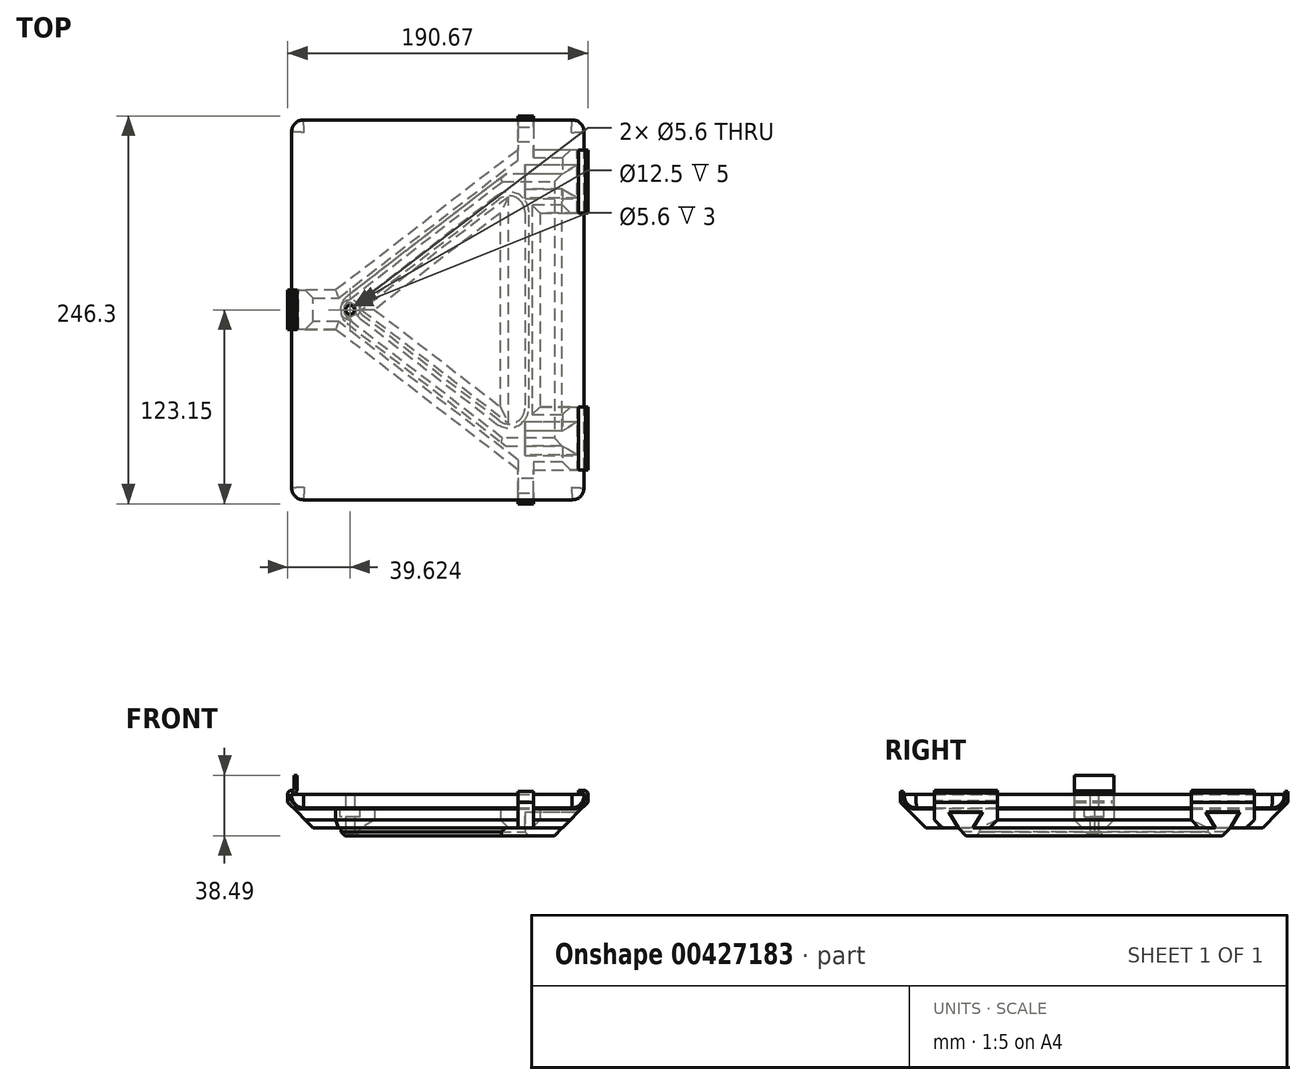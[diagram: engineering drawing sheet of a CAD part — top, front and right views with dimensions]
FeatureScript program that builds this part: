
annotation { "Feature Type Name" : "Feature", "Feature Type Description" : "" }
export const myFeature = defineFeature(function(context is Context, id is Id, definition is map)
    precondition{}
    {
        {
            var Q0;
            Q0=qCreatedBy(makeId("Top.planeOp"),FACE);
            var sketch = newSketch(context, id + "F0", { "sketchPlane" : qUnion([Q0])});
            skLineSegment(sketch, "E0.bottom", {"start": v(0, 0) * mm, "end": v(185.67, 0) * mm});
            skLineSegment(sketch, "E0.top", {"start": v(0, 241.3) * mm, "end": v(185.67, 241.3) * mm});
            skLineSegment(sketch, "E0.left", {"start": v(0, 0) * mm, "end": v(0, 241.3) * mm});
            skLineSegment(sketch, "E0.right", {"start": v(185.67, 0) * mm, "end": v(185.67, 241.3) * mm});
            skSolve(sketch);
        }
        {
            var Q0;
            Q0 = qSketchRegion(id + "F0", true);
            extrude(context, id + "F1", {"entities" : qUnion([Q0]), "depth" : 8.64 * mm});
        }
        {
            var Q0;
            Q0=makeQuery(id+"F1.opExtrude","SWEPT_EDGE",EDGE,{"disambiguationData":[OSD([sQuery(id+"F0.wireOp",EDGE,"E0.top"),sQuery(id+"F0.wireOp",EDGE,"E0.right")])]});
            var Q1;
            Q1=makeQuery(id+"F1.opExtrude","SWEPT_EDGE",EDGE,{"disambiguationData":[OSD([sQuery(id+"F0.wireOp",EDGE,"E0.top"),sQuery(id+"F0.wireOp",EDGE,"E0.left")])]});
            var Q2;
            Q2=makeQuery(id+"F1.opExtrude","SWEPT_EDGE",EDGE,{"disambiguationData":[OSD([sQuery(id+"F0.wireOp",EDGE,"E0.bottom"),sQuery(id+"F0.wireOp",EDGE,"E0.right")])]});
            var Q3;
            Q3=makeQuery(id+"F1.opExtrude","SWEPT_EDGE",EDGE,{"disambiguationData":[OSD([sQuery(id+"F0.wireOp",EDGE,"E0.bottom"),sQuery(id+"F0.wireOp",EDGE,"E0.left")])]});
            fillet(context, id + "F2", {"entities" : qUnion([Q0, Q1, Q2, Q3]), "radius" : 7.5 * mm, "tangentPropagation" : true, "allowEdgeOverflow" : false});
        }
        {
            var Q0;
            Q0=makeQuery(id+"F1.opExtrude","CAP_EDGE",EDGE,{"disambiguationData":[OSD([sQuery(id+"F0.wireOp",EDGE,"E0.right")])],"isStart":true});
            fillet(context, id + "F3", {"entities" : qUnion([Q0]), "radius" : 8 * mm, "tangentPropagation" : true, "allowEdgeOverflow" : false});
        }
        {
            var Q0;
            Q0=qCreatedBy(makeId("Front.planeOp"),FACE);
            cPlane(context, id + "F4", {"entities" : qUnion([Q0]), "cplaneType" : CPlaneType.OFFSET, "offset" : 120.65 * mm, "oppositeDirection" : true, "width" : 150 * mm, "height" : 150 * mm});
        }
        {
            var Q0;
            Q0=qCreatedBy(id+"F4.planeOp",FACE);
            var sketch = newSketch(context, id + "F5", { "sketchPlane" : qUnion([Q0])});
            skLineSegment(sketch, "E1.0.0", {"start": v(178.17, 8.64) * mm, "end": v(7.5, 8.64) * mm, "construction": true});
            skLineSegment(sketch, "E1.0.1", {"start": v(7.5, 8.64) * mm, "end": v(0, 8.64) * mm, "construction": true});
            skLineSegment(sketch, "E1.0.3", {"start": v(0, 8.64) * mm, "end": v(7.5, 8.64) * mm, "construction": true});
            skLineSegment(sketch, "E1.0.4", {"start": v(7.5, 8.64) * mm, "end": v(178.17, 8.64) * mm, "construction": true});
            skLineSegment(sketch, "E1.0.5", {"start": v(178.17, 8.64) * mm, "end": v(185.67, 8.64) * mm, "construction": true});
            skLineSegment(sketch, "E1.0.7", {"start": v(185.67, 8.64) * mm, "end": v(178.17, 8.64) * mm, "construction": true});
            skArc(sketch, "E2.0.0", {"start": v(8, 0) * mm, "mid": v(2.34, 2.34) * mm, "end": v(0, 8) * mm, "construction": true});
            skArc(sketch, "E2.0.2", {"start": v(0, 8) * mm, "mid": v(2.34, 2.34) * mm, "end": v(8, 0) * mm, "construction": true});
            skLineSegment(sketch, "E3.0.0", {"start": v(0, 8.64) * mm, "end": v(0, 8) * mm, "construction": true});
            skLineSegment(sketch, "E3.0.2", {"start": v(0, 8) * mm, "end": v(0, 8.64) * mm, "construction": true});
            skLineSegment(sketch, "E4.0.0", {"start": v(177.67, 0) * mm, "end": v(8, 0) * mm, "construction": true});
            skLineSegment(sketch, "E4.0.2", {"start": v(8, 0) * mm, "end": v(177.67, 0) * mm, "construction": true});
            skLineSegment(sketch, "E5", {"start": v(-0.2, 9.14) * mm, "end": v(1.8, 9.14) * mm});
            skLineSegment(sketch, "E6", {"start": v(-1.04, 11.14) * mm, "end": v(-2.5, 9.67) * mm});
            skLineSegment(sketch, "E7", {"start": v(-2.5, 9.67) * mm, "end": v(-2.5, 3.65) * mm});
            skLineSegment(sketch, "E8", {"start": v(3.65, -2.5) * mm, "end": v(8, -2.5) * mm});
            skLineSegment(sketch, "E9", {"start": v(8, -2.5) * mm, "end": v(8, -0.5) * mm});
            skLineSegment(sketch, "E10", {"start": v(-2.5, 3.65) * mm, "end": v(3.65, -2.5) * mm});
            skLineSegment(sketch, "E11", {"start": v(8, -0.5) * mm, "end": v(4.48, -0.5) * mm});
            skLineSegment(sketch, "E12", {"start": v(4.48, -0.5) * mm, "end": v(-0.5, 4.48) * mm});
            skLineSegment(sketch, "E13", {"start": v(-0.5, 4.48) * mm, "end": v(-0.5, 8.84) * mm});
            skLineSegment(sketch, "E14", {"start": v(-0.5, 8.84) * mm, "end": v(-0.2, 9.14) * mm});
            skLineSegment(sketch, "E15", {"start": v(1.8, 9.14) * mm, "end": v(3.5, 10.84) * mm});
            skLineSegment(sketch, "E16", {"start": v(3.5, 10.84) * mm, "end": v(3.5, 20.84) * mm});
            skLineSegment(sketch, "E17", {"start": v(3.5, 20.84) * mm, "end": v(1.5, 20.84) * mm});
            skLineSegment(sketch, "E18", {"start": v(1.5, 20.84) * mm, "end": v(1.5, 11.67) * mm});
            skLineSegment(sketch, "E19", {"start": v(1.5, 11.67) * mm, "end": v(0.96, 11.14) * mm});
            skLineSegment(sketch, "E20", {"start": v(-1.04, 11.14) * mm, "end": v(0.96, 11.14) * mm});
            skSolve(sketch);
        }
        {
            var Q0;
            Q0 = qSketchRegion(id + "F5", true);
            extrude(context, id + "F6", {"entities" : qUnion([Q0]), "endBound" : BoundingType.SYMMETRIC, "depth" : 25 * mm});
        }
        {
            var Q0;
            Q0=qCreatedBy(makeId("Front.planeOp"),FACE);
            cPlane(context, id + "F7", {"entities" : qUnion([Q0]), "cplaneType" : CPlaneType.OFFSET, "offset" : 19.05 * mm, "oppositeDirection" : true, "width" : 150 * mm, "height" : 150 * mm});
        }
        {
            var Q0;
            Q0=makeQuery(id+"F1.opExtrude","SWEPT_FACE",FACE,{"disambiguationData":[OSD([sQuery(id+"F0.wireOp",EDGE,"E0.top")])]});
            cPlane(context, id + "F8", {"entities" : qUnion([Q0]), "cplaneType" : CPlaneType.OFFSET, "offset" : 19.05 * mm, "oppositeDirection" : true, "width" : 150 * mm, "height" : 150 * mm});
        }
        {
            var Q0;
            Q0=qCreatedBy(id+"F7.planeOp",FACE);
            var sketch = newSketch(context, id + "F9", { "sketchPlane" : qUnion([Q0])});
            skEllipticalArc(sketch, "E21.0.0", {"construction": true});
            skLineSegment(sketch, "E21.0.1", {"start": v(178.17, 8) * mm, "end": v(7.5, 8) * mm, "construction": true});
            skEllipticalArc(sketch, "E21.0.2", {"construction": true});
            skLineSegment(sketch, "E21.0.3", {"start": v(177.67, 0) * mm, "end": v(8, 0) * mm, "construction": true});
            skLineSegment(sketch, "E22", {"start": v(92.84, 0) * mm, "end": v(92.84, 25) * mm, "construction": true});
            skPoint(sketch, "E22.endSnap0", {"position": v(92.84, 8) * mm});
            skLineSegment(sketch, "E23.0.0", {"start": v(8, -0.5) * mm, "end": v(4.48, -0.5) * mm, "construction": true});
            skLineSegment(sketch, "E23.0.1", {"start": v(4.48, -0.5) * mm, "end": v(-0.5, 4.48) * mm, "construction": true});
            skLineSegment(sketch, "E23.0.2", {"start": v(-0.5, 4.48) * mm, "end": v(-0.5, 8.84) * mm, "construction": true});
            skLineSegment(sketch, "E23.0.3", {"start": v(-0.5, 8.84) * mm, "end": v(-0.2, 9.14) * mm, "construction": true});
            skLineSegment(sketch, "E23.0.4", {"start": v(-0.2, 9.14) * mm, "end": v(1.8, 9.14) * mm, "construction": true});
            skLineSegment(sketch, "E23.0.5", {"start": v(1.8, 9.14) * mm, "end": v(3.5, 10.84) * mm, "construction": true});
            skLineSegment(sketch, "E23.0.6", {"start": v(3.5, 10.84) * mm, "end": v(3.5, 20.84) * mm, "construction": true});
            skLineSegment(sketch, "E23.0.7", {"start": v(3.5, 20.84) * mm, "end": v(1.5, 20.84) * mm, "construction": true});
            skLineSegment(sketch, "E23.0.8", {"start": v(1.5, 20.84) * mm, "end": v(1.5, 11.67) * mm, "construction": true});
            skLineSegment(sketch, "E23.0.9", {"start": v(1.5, 11.67) * mm, "end": v(0.96, 11.14) * mm, "construction": true});
            skLineSegment(sketch, "E23.0.10", {"start": v(0.96, 11.14) * mm, "end": v(-1.04, 11.14) * mm, "construction": true});
            skLineSegment(sketch, "E23.0.11", {"start": v(-1.04, 11.14) * mm, "end": v(-2.5, 9.67) * mm, "construction": true});
            skLineSegment(sketch, "E23.0.12", {"start": v(-2.5, 9.67) * mm, "end": v(-2.5, 3.65) * mm, "construction": true});
            skLineSegment(sketch, "E23.0.13", {"start": v(-2.5, 3.65) * mm, "end": v(3.65, -2.5) * mm, "construction": true});
            skLineSegment(sketch, "E23.0.14", {"start": v(3.65, -2.5) * mm, "end": v(8, -2.5) * mm, "construction": true});
            skLineSegment(sketch, "E23.0.15", {"start": v(8, -2.5) * mm, "end": v(8, -0.5) * mm, "construction": true});
            skLineSegment(sketch, "E24.MirrorCS", {"start": v(186.17, 8.84) * mm, "end": v(185.88, 9.14) * mm});
            skLineSegment(sketch, "E25.MirrorCS", {"start": v(185.88, 9.14) * mm, "end": v(184.7, 9.14) * mm});
            skLineSegment(sketch, "E26.MirrorCS", {"start": v(177.67, -2.5) * mm, "end": v(177.67, -0.5) * mm});
            skLineSegment(sketch, "E27.MirrorCS", {"start": v(177.67, -0.5) * mm, "end": v(181.2, -0.5) * mm});
            skLineSegment(sketch, "E28.MirrorCS", {"start": v(186.7, 11.14) * mm, "end": v(188.17, 9.67) * mm});
            skLineSegment(sketch, "E29.MirrorCS", {"start": v(184.7, 11.14) * mm, "end": v(186.7, 11.14) * mm});
            skLineSegment(sketch, "E30.MirrorCS", {"start": v(188.17, 9.67) * mm, "end": v(188.17, 3.65) * mm});
            skLineSegment(sketch, "E31.MirrorCS", {"start": v(181.2, -0.5) * mm, "end": v(186.17, 4.48) * mm});
            skLineSegment(sketch, "E32.MirrorCS", {"start": v(182.02, -2.5) * mm, "end": v(177.67, -2.5) * mm});
            skLineSegment(sketch, "E33.MirrorCS", {"start": v(188.17, 3.65) * mm, "end": v(182.02, -2.5) * mm});
            skLineSegment(sketch, "E34.MirrorCS", {"start": v(186.17, 4.48) * mm, "end": v(186.17, 8.84) * mm});
            skEllipticalArc(sketch, "E35.MirrorCS", {"construction": true});
            skLineSegment(sketch, "E36", {"start": v(184.7, 11.14) * mm, "end": v(184.7, 9.14) * mm});
            skPoint(sketch, "E37.MirrorCS.end.orphan", {"position": v(184.17, 11.67) * mm});
            skPoint(sketch, "E38.MirrorCS.start.orphan", {"position": v(183.88, 9.14) * mm});
            skPoint(sketch, "E39.MirrorCS.end.orphan", {"position": v(184.17, 20.84) * mm});
            skPoint(sketch, "E40.MirrorCS.end.orphan", {"position": v(182.17, 20.84) * mm});
            skPoint(sketch, "E40.MirrorCS.start.orphan", {"position": v(182.17, 10.84) * mm});
            const initialGuessF9  = {"E21.0.0": [0.177674, 0.008, 0, 1, 0.008, 0.0005, 3.141592653589793, 4.71238898038469], "E21.0.2": [0.008, 0.008, 0, -1, 0.008, 0.0005, 4.71238898038469, 0], "E35.MirrorCS": [0.177674, 0.008, 0, -1, 0.008, 0.0005, 0, 1.5707963267948966]};
            skSetInitialGuess(sketch, initialGuessF9);
            skSolve(sketch);
        }
        {
            var Q0;
            Q0=qCreatedBy(id+"F8.planeOp",FACE);
            var sketch = newSketch(context, id + "F10", { "sketchPlane" : qUnion([Q0])});
            skLineSegment(sketch, "E41.0.0", {"start": v(-177.67, -2.5) * mm, "end": v(-182.02, -2.5) * mm});
            skLineSegment(sketch, "E41.0.1", {"start": v(-182.02, -2.5) * mm, "end": v(-188.17, 3.65) * mm});
            skLineSegment(sketch, "E41.0.2", {"start": v(-188.17, 3.65) * mm, "end": v(-188.17, 9.67) * mm});
            skLineSegment(sketch, "E41.0.3", {"start": v(-188.17, 9.67) * mm, "end": v(-186.7, 11.14) * mm});
            skLineSegment(sketch, "E41.0.4", {"start": v(-186.7, 11.14) * mm, "end": v(-184.7, 11.14) * mm});
            skLineSegment(sketch, "E41.0.5", {"start": v(-184.7, 11.14) * mm, "end": v(-184.7, 9.14) * mm});
            skLineSegment(sketch, "E41.0.6", {"start": v(-184.7, 9.14) * mm, "end": v(-185.88, 9.14) * mm});
            skLineSegment(sketch, "E41.0.7", {"start": v(-185.88, 9.14) * mm, "end": v(-186.17, 8.84) * mm});
            skLineSegment(sketch, "E41.0.8", {"start": v(-186.17, 8.84) * mm, "end": v(-186.17, 4.48) * mm});
            skLineSegment(sketch, "E41.0.9", {"start": v(-186.17, 4.48) * mm, "end": v(-181.2, -0.5) * mm});
            skLineSegment(sketch, "E41.0.10", {"start": v(-181.2, -0.5) * mm, "end": v(-177.67, -0.5) * mm});
            skLineSegment(sketch, "E41.0.11", {"start": v(-177.67, -0.5) * mm, "end": v(-177.67, -2.5) * mm});
            skSolve(sketch);
        }
        {
            var Q0;
            Q0 = qSketchRegion(id + "F9", true);
            extrude(context, id + "F11", {"entities" : qUnion([Q0]), "oppositeDirection" : true, "depth" : 40 * mm});
        }
        {
            var Q0;
            Q0 = qSketchRegion(id + "F10", true);
            extrude(context, id + "F12", {"entities" : qUnion([Q0]), "oppositeDirection" : true, "depth" : 40 * mm});
        }
        {
            var Q0;
            Q0=makeQuery(id+"F6.opExtrude","SWEPT_FACE",FACE,{"disambiguationData":[OSD([sQuery(id+"F5.wireOp",EDGE,"E8")])]});
            var sketch = newSketch(context, id + "F13", { "sketchPlane" : qUnion([Q0])});
            skLineSegment(sketch, "E42.0", {"start": v(177.67, -59.05) * mm, "end": v(177.67, -19.05) * mm});
            skLineSegment(sketch, "E43.0", {"start": v(177.67, -182.25) * mm, "end": v(177.67, -222.25) * mm});
            skLineSegment(sketch, "E44.0", {"start": v(8, -108.15) * mm, "end": v(8, -133.15) * mm});
            skLineSegment(sketch, "E45", {"start": v(8, -108.15) * mm, "end": v(28, -108.15) * mm});
            skLineSegment(sketch, "E46", {"start": v(28, -108.15) * mm, "end": v(143.62, -19.05) * mm});
            skLineSegment(sketch, "E47", {"start": v(143.62, -19.05) * mm, "end": v(177.67, -19.05) * mm});
            skLineSegment(sketch, "E48", {"start": v(177.67, -59.05) * mm, "end": v(157.67, -59.05) * mm});
            skLineSegment(sketch, "E49", {"start": v(157.67, -59.05) * mm, "end": v(157.67, -182.25) * mm});
            skLineSegment(sketch, "E50", {"start": v(177.67, -182.25) * mm, "end": v(157.67, -182.25) * mm});
            skLineSegment(sketch, "E51", {"start": v(8, -133.15) * mm, "end": v(28, -133.15) * mm});
            skLineSegment(sketch, "E52", {"start": v(28, -133.15) * mm, "end": v(143.62, -222.25) * mm});
            skLineSegment(sketch, "E53", {"start": v(143.62, -222.25) * mm, "end": v(177.67, -222.25) * mm});
            skLineSegment(sketch, "E54", {"start": v(132.67, -59.05) * mm, "end": v(52.74, -120.65) * mm});
            skLineSegment(sketch, "E55", {"start": v(52.74, -120.65) * mm, "end": v(132.67, -182.25) * mm});
            skLineSegment(sketch, "E56", {"start": v(132.67, -182.25) * mm, "end": v(132.67, -59.05) * mm});
            skSolve(sketch);
        }
        {
            var Q0;
            Q0 = qSketchRegion(id + "F13", true);
            var Q1;
            Q1=makeQuery(id+"F6.opExtrude","SWEPT_FACE",FACE,{"disambiguationData":[OSD([sQuery(id+"F5.wireOp",EDGE,"E11")])]});
            extrude(context, id + "F14", {"entities" : qUnion([Q0]), "operationType" : NewBodyOperationType.ADD, "endBound" : BoundingType.UP_TO_SURFACE, "oppositeDirection" : true, "endBoundEntityFace" : qUnion([Q1]), "depth" : 25 * mm});
        }
        {
            var Q0;
            Q0=makeQuery(id+"F14.boolean.opBoolean","MERGE",FACE,{"derivedFrom":[makeQuery(id+"F6.opExtrude","SWEPT_FACE",FACE,{"disambiguationData":[OSD([sQuery(id+"F5.wireOp",EDGE,"E8")])]}),makeQuery(id+"F11.opExtrude","SWEPT_FACE",FACE,{"disambiguationData":[OSD([sQuery(id+"F9.wireOp",EDGE,"E32.MirrorCS")])]}),makeQuery(id+"F12.opExtrude","SWEPT_FACE",FACE,{"disambiguationData":[OSD([sQuery(id+"F10.wireOp",EDGE,"E41.0.0")])]}),makeQuery(id+"F14.opExtrude","CAP_FACE",FACE,{"disambiguationData":[OSD([sQuery(id+"F13.wireOp",EDGE,"E42.0"),sQuery(id+"F13.wireOp",EDGE,"E43.0"),sQuery(id+"F13.wireOp",EDGE,"E44.0"),sQuery(id+"F13.wireOp",EDGE,"E45"),sQuery(id+"F13.wireOp",EDGE,"E46"),sQuery(id+"F13.wireOp",EDGE,"E47"),sQuery(id+"F13.wireOp",EDGE,"E48"),sQuery(id+"F13.wireOp",EDGE,"E49"),sQuery(id+"F13.wireOp",EDGE,"E50"),sQuery(id+"F13.wireOp",EDGE,"E51"),sQuery(id+"F13.wireOp",EDGE,"E52"),sQuery(id+"F13.wireOp",EDGE,"E53"),sQuery(id+"F13.wireOp",EDGE,"E54"),sQuery(id+"F13.wireOp",EDGE,"E55"),sQuery(id+"F13.wireOp",EDGE,"E56")])],"isStart":true})]});
            var sketch = newSketch(context, id + "F15", { "sketchPlane" : qUnion([Q0])});
            skLineSegment(sketch, "E57.bottom", {"start": v(143.62, -19.05) * mm, "end": v(153.62, -19.05) * mm});
            skLineSegment(sketch, "E57.top", {"start": v(143.62, -8) * mm, "end": v(153.62, -8) * mm});
            skLineSegment(sketch, "E57.left", {"start": v(143.62, -19.05) * mm, "end": v(143.62, -8) * mm});
            skLineSegment(sketch, "E57.right", {"start": v(153.62, -19.05) * mm, "end": v(153.62, -8) * mm});
            skLineSegment(sketch, "E58.bottom", {"start": v(143.62, -222.25) * mm, "end": v(153.62, -222.25) * mm});
            skLineSegment(sketch, "E58.top", {"start": v(143.62, -233.3) * mm, "end": v(153.62, -233.3) * mm});
            skLineSegment(sketch, "E58.left", {"start": v(143.62, -222.25) * mm, "end": v(143.62, -233.3) * mm});
            skLineSegment(sketch, "E58.right", {"start": v(153.62, -222.25) * mm, "end": v(153.62, -233.3) * mm});
            skSolve(sketch);
        }
        {
            var Q0;
            Q0 = qSketchRegion(id + "F15", true);
            var Q1;
            Q1=makeQuery(id+"F14.boolean.opBoolean","MERGE",FACE,{"derivedFrom":[makeQuery(id+"F6.opExtrude","SWEPT_FACE",FACE,{"disambiguationData":[OSD([sQuery(id+"F5.wireOp",EDGE,"E11")])]}),makeQuery(id+"F11.opExtrude","SWEPT_FACE",FACE,{"disambiguationData":[OSD([sQuery(id+"F9.wireOp",EDGE,"E27.MirrorCS")])]}),makeQuery(id+"F12.opExtrude","SWEPT_FACE",FACE,{"disambiguationData":[OSD([sQuery(id+"F10.wireOp",EDGE,"E41.0.10")])]}),makeQuery(id+"F14.opExtrude","CAP_FACE",FACE,{"disambiguationData":[OSD([sQuery(id+"F13.wireOp",EDGE,"E42.0"),sQuery(id+"F13.wireOp",EDGE,"E43.0"),sQuery(id+"F13.wireOp",EDGE,"E44.0"),sQuery(id+"F13.wireOp",EDGE,"E45"),sQuery(id+"F13.wireOp",EDGE,"E46"),sQuery(id+"F13.wireOp",EDGE,"E47"),sQuery(id+"F13.wireOp",EDGE,"E48"),sQuery(id+"F13.wireOp",EDGE,"E49"),sQuery(id+"F13.wireOp",EDGE,"E50"),sQuery(id+"F13.wireOp",EDGE,"E51"),sQuery(id+"F13.wireOp",EDGE,"E52"),sQuery(id+"F13.wireOp",EDGE,"E53"),sQuery(id+"F13.wireOp",EDGE,"E54"),sQuery(id+"F13.wireOp",EDGE,"E55"),sQuery(id+"F13.wireOp",EDGE,"E56")])],"isStart":false})]});
            extrude(context, id + "F16", {"entities" : qUnion([Q0]), "operationType" : NewBodyOperationType.ADD, "endBound" : BoundingType.UP_TO_SURFACE, "oppositeDirection" : true, "endBoundEntityFace" : qUnion([Q1]), "depth" : 25 * mm});
        }
        {
            var Q0;
            Q0=makeQuery(id+"F16.opExtrude","SWEPT_FACE",FACE,{"disambiguationData":[OSD([sQuery(id+"F15.wireOp",EDGE,"E57.right")])]});
            var sketch = newSketch(context, id + "F17", { "sketchPlane" : qUnion([Q0])});
            skLineSegment(sketch, "E59", {"start": v(8, -0.5) * mm, "end": v(4.48, -0.5) * mm});
            skLineSegment(sketch, "E60", {"start": v(4.48, -0.5) * mm, "end": v(-0.5, 4.48) * mm});
            skLineSegment(sketch, "E61", {"start": v(-0.5, 4.48) * mm, "end": v(-0.5, 10.64) * mm});
            skLineSegment(sketch, "E62", {"start": v(-0.5, 10.64) * mm, "end": v(-2.5, 10.64) * mm});
            skLineSegment(sketch, "E63", {"start": v(-2.5, 10.64) * mm, "end": v(-2.5, 3.65) * mm});
            skLineSegment(sketch, "E64", {"start": v(-2.5, 3.65) * mm, "end": v(3.65, -2.5) * mm});
            skLineSegment(sketch, "E65", {"start": v(8, -2.5) * mm, "end": v(3.65, -2.5) * mm});
            skPoint(sketch, "E66.0", {"position": v(8, -1.5) * mm});
            skLineSegment(sketch, "E67.0", {"start": v(8, -0.5) * mm, "end": v(8, -2.5) * mm});
            skLineSegment(sketch, "E68.0.0", {"start": v(182.25, -2.5) * mm, "end": v(182.25, -0.5) * mm, "construction": true});
            skLineSegment(sketch, "E68.0.1", {"start": v(182.25, -0.5) * mm, "end": v(59.05, -0.5) * mm, "construction": true});
            skLineSegment(sketch, "E68.0.2", {"start": v(59.05, -0.5) * mm, "end": v(59.05, -2.5) * mm, "construction": true});
            skLineSegment(sketch, "E68.0.3", {"start": v(59.05, -2.5) * mm, "end": v(182.25, -2.5) * mm, "construction": true});
            skLineSegment(sketch, "E69", {"start": v(120.65, -2.5) * mm, "end": v(120.65, 22.5) * mm, "construction": true});
            skPoint(sketch, "E69.endSnap0", {"position": v(120.65, -0.5) * mm});
            skLineSegment(sketch, "E70.MirrorCS", {"start": v(233.3, -0.5) * mm, "end": v(233.3, -2.5) * mm});
            skLineSegment(sketch, "E71.MirrorCS", {"start": v(241.8, 10.64) * mm, "end": v(243.8, 10.64) * mm});
            skPoint(sketch, "E72.MirrorP", {"position": v(233.3, -1.5) * mm});
            skLineSegment(sketch, "E73.MirrorCS", {"start": v(243.8, 3.65) * mm, "end": v(237.65, -2.5) * mm});
            skLineSegment(sketch, "E74.MirrorCS", {"start": v(243.8, 10.64) * mm, "end": v(243.8, 3.65) * mm});
            skLineSegment(sketch, "E75.MirrorCS", {"start": v(233.3, -0.5) * mm, "end": v(236.82, -0.5) * mm});
            skLineSegment(sketch, "E76.MirrorCS", {"start": v(241.8, 4.48) * mm, "end": v(241.8, 10.64) * mm});
            skLineSegment(sketch, "E77.MirrorCS", {"start": v(233.3, -2.5) * mm, "end": v(237.65, -2.5) * mm});
            skLineSegment(sketch, "E78.MirrorCS", {"start": v(236.82, -0.5) * mm, "end": v(241.8, 4.48) * mm});
            skSolve(sketch);
        }
        {
            var Q0;
            Q0 = qSketchRegion(id + "F17", true);
            var Q1;
            Q1=makeQuery(id+"F16.opExtrude","SWEPT_FACE",FACE,{"disambiguationData":[OSD([sQuery(id+"F15.wireOp",EDGE,"E57.left")])]});
            extrude(context, id + "F18", {"entities" : qUnion([Q0]), "operationType" : NewBodyOperationType.ADD, "endBound" : BoundingType.UP_TO_SURFACE, "oppositeDirection" : true, "endBoundEntityFace" : qUnion([Q1]), "depth" : 25 * mm});
        }
        {
            var Q0;
            Q0=makeQuery(id+"F18.boolean.opBoolean","MERGE",FACE,{"derivedFrom":[makeQuery(id+"F16.boolean.opBoolean","MERGE",FACE,{"derivedFrom":[makeQuery(id+"F14.boolean.opBoolean","MERGE",FACE,{"derivedFrom":[makeQuery(id+"F6.opExtrude","SWEPT_FACE",FACE,{"disambiguationData":[OSD([sQuery(id+"F5.wireOp",EDGE,"E8")])]}),makeQuery(id+"F11.opExtrude","SWEPT_FACE",FACE,{"disambiguationData":[OSD([sQuery(id+"F9.wireOp",EDGE,"E32.MirrorCS")])]}),makeQuery(id+"F12.opExtrude","SWEPT_FACE",FACE,{"disambiguationData":[OSD([sQuery(id+"F10.wireOp",EDGE,"E41.0.0")])]}),makeQuery(id+"F14.opExtrude","CAP_FACE",FACE,{"disambiguationData":[OSD([sQuery(id+"F13.wireOp",EDGE,"E42.0"),sQuery(id+"F13.wireOp",EDGE,"E43.0"),sQuery(id+"F13.wireOp",EDGE,"E44.0"),sQuery(id+"F13.wireOp",EDGE,"E45"),sQuery(id+"F13.wireOp",EDGE,"E46"),sQuery(id+"F13.wireOp",EDGE,"E47"),sQuery(id+"F13.wireOp",EDGE,"E48"),sQuery(id+"F13.wireOp",EDGE,"E49"),sQuery(id+"F13.wireOp",EDGE,"E50"),sQuery(id+"F13.wireOp",EDGE,"E51"),sQuery(id+"F13.wireOp",EDGE,"E52"),sQuery(id+"F13.wireOp",EDGE,"E53"),sQuery(id+"F13.wireOp",EDGE,"E54"),sQuery(id+"F13.wireOp",EDGE,"E55"),sQuery(id+"F13.wireOp",EDGE,"E56")])],"isStart":true})]}),makeQuery(id+"F16.opExtrude","CAP_FACE",FACE,{"disambiguationData":[OSD([sQuery(id+"F15.wireOp",EDGE,"E57.bottom"),sQuery(id+"F15.wireOp",EDGE,"E57.top"),sQuery(id+"F15.wireOp",EDGE,"E57.left"),sQuery(id+"F15.wireOp",EDGE,"E57.right")])],"isStart":true}),makeQuery(id+"F16.opExtrude","CAP_FACE",FACE,{"disambiguationData":[OSD([sQuery(id+"F15.wireOp",EDGE,"E58.bottom"),sQuery(id+"F15.wireOp",EDGE,"E58.top"),sQuery(id+"F15.wireOp",EDGE,"E58.left"),sQuery(id+"F15.wireOp",EDGE,"E58.right")])],"isStart":true})]}),makeQuery(id+"F18.opExtrude","SWEPT_FACE",FACE,{"disambiguationData":[OSD([sQuery(id+"F17.wireOp",EDGE,"E65")])]}),makeQuery(id+"F18.opExtrude","SWEPT_FACE",FACE,{"disambiguationData":[OSD([sQuery(id+"F17.wireOp",EDGE,"E77.MirrorCS")])]})]});
            extrude(context, id + "F19", {"entities" : qUnion([Q0]), "operationType" : NewBodyOperationType.ADD, "depth" : 10 * mm});
        }
        {
            var Q0;
            Q0=makeQuery(id+"F19.opExtrude","CAP_EDGE",EDGE,{"disambiguationData":[OSD([sQuery(id+"F5.wireOp",EDGE,"E8"),sQuery(id+"F5.wireOp",EDGE,"E10")])],"isStart":false});
            var Q1;
            Q1=makeQuery(id+"F19.opExtrude","CAP_EDGE",EDGE,{"disambiguationData":[OSD([sQuery(id+"F17.wireOp",EDGE,"E73.MirrorCS"),sQuery(id+"F17.wireOp",EDGE,"E77.MirrorCS")])],"isStart":false});
            var Q2;
            Q2=makeQuery(id+"F19.opExtrude","CAP_EDGE",EDGE,{"disambiguationData":[OSD([sQuery(id+"F10.wireOp",EDGE,"E41.0.0"),sQuery(id+"F10.wireOp",EDGE,"E41.0.1")])],"isStart":false});
            var Q3;
            Q3=makeQuery(id+"F19.opExtrude","CAP_EDGE",EDGE,{"disambiguationData":[OSD([sQuery(id+"F17.wireOp",EDGE,"E64"),sQuery(id+"F17.wireOp",EDGE,"E65")])],"isStart":false});
            var Q4;
            Q4=makeQuery(id+"F19.opExtrude","CAP_EDGE",EDGE,{"disambiguationData":[OSD([sQuery(id+"F9.wireOp",EDGE,"E32.MirrorCS"),sQuery(id+"F9.wireOp",EDGE,"E33.MirrorCS")])],"isStart":false});
            chamfer(context, id + "F20", {"entities" : qUnion([Q0, Q1, Q2, Q3, Q4]), "width" : 10 * mm, "tangentPropagation" : true});
        }
        {
            var Q0;
            Q0=makeQuery(id+"F19.opExtrude","CAP_EDGE",EDGE,{"disambiguationData":[OSD([sQuery(id+"F13.wireOp",EDGE,"E55")])],"isStart":false});
            var Q1;
            Q1=makeQuery(id+"F19.opExtrude","CAP_EDGE",EDGE,{"disambiguationData":[OSD([sQuery(id+"F13.wireOp",EDGE,"E49")])],"isStart":false});
            var Q2;
            Q2=makeQuery(id+"F19.opExtrude","CAP_EDGE",EDGE,{"disambiguationData":[OSD([sQuery(id+"F13.wireOp",EDGE,"E46")])],"isStart":false});
            var Q3;
            Q3=makeQuery(id+"F19.opExtrude","CAP_EDGE",EDGE,{"disambiguationData":[OSD([sQuery(id+"F13.wireOp",EDGE,"E52")])],"isStart":false});
            var Q4;
            Q4=makeQuery(id+"F19.opExtrude","CAP_EDGE",EDGE,{"disambiguationData":[OSD([sQuery(id+"F13.wireOp",EDGE,"E56")])],"isStart":false});
            var Q5;
            Q5=makeQuery(id+"F19.opExtrude","CAP_EDGE",EDGE,{"disambiguationData":[OSD([sQuery(id+"F13.wireOp",EDGE,"E54")])],"isStart":false});
            var Q6;
            Q6=makeQuery(id+"F19.opExtrude","CAP_EDGE",EDGE,{"disambiguationData":[OSD([sQuery(id+"F10.wireOp",EDGE,"E41.0.0"),sQuery(id+"F13.wireOp",EDGE,"E50")])],"isStart":false});
            var Q7;
            Q7=makeQuery(id+"F19.opExtrude","CAP_EDGE",EDGE,{"disambiguationData":[OSD([sQuery(id+"F10.wireOp",EDGE,"E41.0.0"),sQuery(id+"F13.wireOp",EDGE,"E53")])],"isStart":false});
            var Q8;
            Q8=makeQuery(id+"F19.opExtrude","CAP_EDGE",EDGE,{"disambiguationData":[OSD([sQuery(id+"F9.wireOp",EDGE,"E32.MirrorCS"),sQuery(id+"F13.wireOp",EDGE,"E48")])],"isStart":false});
            var Q9;
            Q9=makeQuery(id+"F19.opExtrude","CAP_EDGE",EDGE,{"disambiguationData":[OSD([sQuery(id+"F9.wireOp",EDGE,"E32.MirrorCS"),sQuery(id+"F13.wireOp",EDGE,"E47")])],"isStart":false});
            var Q10;
            Q10=makeQuery(id+"F19.opExtrude","CAP_EDGE",EDGE,{"disambiguationData":[OSD([sQuery(id+"F5.wireOp",EDGE,"E8"),sQuery(id+"F13.wireOp",EDGE,"E51")])],"isStart":false});
            var Q11;
            Q11=makeQuery(id+"F19.opExtrude","CAP_EDGE",EDGE,{"disambiguationData":[OSD([sQuery(id+"F5.wireOp",EDGE,"E8"),sQuery(id+"F13.wireOp",EDGE,"E45")])],"isStart":false});
            chamfer(context, id + "F21", {"entities" : qUnion([Q0, Q1, Q2, Q3, Q4, Q5, Q6, Q7, Q8, Q9, Q10, Q11]), "width" : 5 * mm, "tangentPropagation" : true});
        }
        {
            var Q0;
            Q0=makeQuery(id+"F12.opExtrude","SWEPT_FACE",FACE,{"disambiguationData":[OSD([sQuery(id+"F10.wireOp",EDGE,"E41.0.2")])]});
            var sketch = newSketch(context, id + "F22", { "sketchPlane" : qUnion([Q0])});
            skLineSegment(sketch, "E79.0.0", {"start": v(187.25, -12.5) * mm, "end": v(217.25, -12.5) * mm, "construction": true});
            skLineSegment(sketch, "E79.0.1", {"start": v(217.25, -12.5) * mm, "end": v(222.25, -7.5) * mm, "construction": true});
            skLineSegment(sketch, "E79.0.2", {"start": v(222.25, -7.5) * mm, "end": v(222.25, -2.5) * mm, "construction": true});
            skLineSegment(sketch, "E79.0.3", {"start": v(222.25, -2.5) * mm, "end": v(222.25, 3.65) * mm, "construction": true});
            skLineSegment(sketch, "E79.0.4", {"start": v(222.25, 3.65) * mm, "end": v(182.25, 3.65) * mm, "construction": true});
            skLineSegment(sketch, "E79.0.5", {"start": v(182.25, 3.65) * mm, "end": v(182.25, -2.5) * mm, "construction": true});
            skLineSegment(sketch, "E79.0.6", {"start": v(182.25, -2.5) * mm, "end": v(182.25, -7.5) * mm, "construction": true});
            skLineSegment(sketch, "E79.0.7", {"start": v(182.25, -7.5) * mm, "end": v(187.25, -12.5) * mm, "construction": true});
            skLineSegment(sketch, "E80", {"start": v(207.25, -12.5) * mm, "end": v(213.02, -2.5) * mm});
            skLineSegment(sketch, "E81", {"start": v(191.48, -2.5) * mm, "end": v(197.25, -12.5) * mm});
            skLineSegment(sketch, "E82", {"start": v(207.25, -12.5) * mm, "end": v(197.25, -12.5) * mm});
            skLineSegment(sketch, "E83.0.0", {"start": v(19.05, -7.5) * mm, "end": v(19.05, -2.5) * mm, "construction": true});
            skLineSegment(sketch, "E83.0.1", {"start": v(19.05, -7.5) * mm, "end": v(24.05, -12.5) * mm, "construction": true});
            skLineSegment(sketch, "E83.0.2", {"start": v(24.05, -12.5) * mm, "end": v(54.05, -12.5) * mm, "construction": true});
            skLineSegment(sketch, "E83.0.3", {"start": v(54.05, -12.5) * mm, "end": v(59.05, -7.5) * mm, "construction": true});
            skLineSegment(sketch, "E83.0.4", {"start": v(59.05, -2.5) * mm, "end": v(59.05, -7.5) * mm, "construction": true});
            skLineSegment(sketch, "E83.0.5", {"start": v(59.05, -2.5) * mm, "end": v(59.05, 3.65) * mm, "construction": true});
            skLineSegment(sketch, "E83.0.6", {"start": v(59.05, 3.65) * mm, "end": v(19.05, 3.65) * mm, "construction": true});
            skLineSegment(sketch, "E83.0.7", {"start": v(19.05, 3.65) * mm, "end": v(19.05, -2.5) * mm, "construction": true});
            skLineSegment(sketch, "E84", {"start": v(44.05, -12.5) * mm, "end": v(49.82, -2.5) * mm});
            skLineSegment(sketch, "E85", {"start": v(34.05, -12.5) * mm, "end": v(28.28, -2.5) * mm});
            skLineSegment(sketch, "E86", {"start": v(44.05, -12.5) * mm, "end": v(34.05, -12.5) * mm});
            skLineSegment(sketch, "E87", {"start": v(28.28, -2.5) * mm, "end": v(49.82, -2.5) * mm});
            skLineSegment(sketch, "E88", {"start": v(213.02, -2.5) * mm, "end": v(191.48, -2.5) * mm});
            skSolve(sketch);
        }
        {
            var Q0;
            Q0 = qSketchRegion(id + "F22", true);
            extrude(context, id + "F23", {"entities" : qUnion([Q0]), "operationType" : NewBodyOperationType.REMOVE, "oppositeDirection" : true, "depth" : 40 * mm});
        }
        {
            var Q0;
            Q0=makeQuery(id+"F19.opExtrude","CAP_FACE",FACE,{"disambiguationData":[OSD([sQuery(id+"F5.wireOp",EDGE,"E8"),sQuery(id+"F9.wireOp",EDGE,"E32.MirrorCS"),sQuery(id+"F10.wireOp",EDGE,"E41.0.0"),sQuery(id+"F13.wireOp",EDGE,"E42.0"),sQuery(id+"F13.wireOp",EDGE,"E43.0"),sQuery(id+"F13.wireOp",EDGE,"E44.0"),sQuery(id+"F13.wireOp",EDGE,"E45"),sQuery(id+"F13.wireOp",EDGE,"E46"),sQuery(id+"F13.wireOp",EDGE,"E47"),sQuery(id+"F13.wireOp",EDGE,"E48"),sQuery(id+"F13.wireOp",EDGE,"E49"),sQuery(id+"F13.wireOp",EDGE,"E50"),sQuery(id+"F13.wireOp",EDGE,"E51"),sQuery(id+"F13.wireOp",EDGE,"E52"),sQuery(id+"F13.wireOp",EDGE,"E53"),sQuery(id+"F13.wireOp",EDGE,"E54"),sQuery(id+"F13.wireOp",EDGE,"E55"),sQuery(id+"F13.wireOp",EDGE,"E56"),sQuery(id+"F15.wireOp",EDGE,"E57.bottom"),sQuery(id+"F15.wireOp",EDGE,"E57.top"),sQuery(id+"F15.wireOp",EDGE,"E57.left"),sQuery(id+"F15.wireOp",EDGE,"E57.right"),sQuery(id+"F15.wireOp",EDGE,"E58.bottom"),sQuery(id+"F15.wireOp",EDGE,"E58.top"),sQuery(id+"F15.wireOp",EDGE,"E58.left"),sQuery(id+"F15.wireOp",EDGE,"E58.right"),sQuery(id+"F17.wireOp",EDGE,"E65"),sQuery(id+"F17.wireOp",EDGE,"E77.MirrorCS")])],"isStart":false});
            var sketch = newSketch(context, id + "F24", { "sketchPlane" : qUnion([Q0])});
            skCircle(sketch, "E89", {"center": v(37.12, -120.65) * mm, "radius": 2.8 * mm});
            skSolve(sketch);
        }
        {
            var Q0;
            Q0 = qSketchRegion(id + "F24", true);
            extrude(context, id + "F25", {"entities" : qUnion([Q0]), "operationType" : NewBodyOperationType.REMOVE, "endBound" : BoundingType.THROUGH_ALL, "oppositeDirection" : true, "depth" : 25 * mm});
        }
        {
            var Q0;
            Q0=makeQuery(id+"F18.boolean.opBoolean","MERGE",FACE,{"derivedFrom":[makeQuery(id+"F16.boolean.opBoolean","MERGE",FACE,{"derivedFrom":[makeQuery(id+"F14.boolean.opBoolean","MERGE",FACE,{"derivedFrom":[makeQuery(id+"F6.opExtrude","SWEPT_FACE",FACE,{"disambiguationData":[OSD([sQuery(id+"F5.wireOp",EDGE,"E11")])]}),makeQuery(id+"F11.opExtrude","SWEPT_FACE",FACE,{"disambiguationData":[OSD([sQuery(id+"F9.wireOp",EDGE,"E27.MirrorCS")])]}),makeQuery(id+"F12.opExtrude","SWEPT_FACE",FACE,{"disambiguationData":[OSD([sQuery(id+"F10.wireOp",EDGE,"E41.0.10")])]}),makeQuery(id+"F14.opExtrude","CAP_FACE",FACE,{"disambiguationData":[OSD([sQuery(id+"F13.wireOp",EDGE,"E42.0"),sQuery(id+"F13.wireOp",EDGE,"E43.0"),sQuery(id+"F13.wireOp",EDGE,"E44.0"),sQuery(id+"F13.wireOp",EDGE,"E45"),sQuery(id+"F13.wireOp",EDGE,"E46"),sQuery(id+"F13.wireOp",EDGE,"E47"),sQuery(id+"F13.wireOp",EDGE,"E48"),sQuery(id+"F13.wireOp",EDGE,"E49"),sQuery(id+"F13.wireOp",EDGE,"E50"),sQuery(id+"F13.wireOp",EDGE,"E51"),sQuery(id+"F13.wireOp",EDGE,"E52"),sQuery(id+"F13.wireOp",EDGE,"E53"),sQuery(id+"F13.wireOp",EDGE,"E54"),sQuery(id+"F13.wireOp",EDGE,"E55"),sQuery(id+"F13.wireOp",EDGE,"E56")])],"isStart":false})]}),makeQuery(id+"F16.opExtrude","CAP_FACE",FACE,{"disambiguationData":[OSD([sQuery(id+"F15.wireOp",EDGE,"E57.bottom"),sQuery(id+"F15.wireOp",EDGE,"E57.top"),sQuery(id+"F15.wireOp",EDGE,"E57.left"),sQuery(id+"F15.wireOp",EDGE,"E57.right")])],"isStart":false}),makeQuery(id+"F16.opExtrude","CAP_FACE",FACE,{"disambiguationData":[OSD([sQuery(id+"F15.wireOp",EDGE,"E58.bottom"),sQuery(id+"F15.wireOp",EDGE,"E58.top"),sQuery(id+"F15.wireOp",EDGE,"E58.left"),sQuery(id+"F15.wireOp",EDGE,"E58.right")])],"isStart":false})]}),makeQuery(id+"F18.opExtrude","SWEPT_FACE",FACE,{"disambiguationData":[OSD([sQuery(id+"F17.wireOp",EDGE,"E59")])]}),makeQuery(id+"F18.opExtrude","SWEPT_FACE",FACE,{"disambiguationData":[OSD([sQuery(id+"F17.wireOp",EDGE,"E75.MirrorCS")])]})]});
            var sketch = newSketch(context, id + "F26", { "sketchPlane" : qUnion([Q0])});
            skCircle(sketch, "E90", {"center": v(37.12, 120.65) * mm, "radius": 6.25 * mm});
            skSolve(sketch);
        }
        {
            var Q0;
            Q0 = qSketchRegion(id + "F26", true);
            extrude(context, id + "F27", {"entities" : qUnion([Q0]), "operationType" : NewBodyOperationType.REMOVE, "oppositeDirection" : true, "depth" : 5 * mm});
        }
        {
            var Q0;
            Q0=makeQuery(id+"F23.boolean.opBoolean","COPY",FACE,{"derivedFrom":makeQuery(id+"F23.opExtrude","CAP_FACE",FACE,{"disambiguationData":[OSD([sQuery(id+"F22.wireOp",EDGE,"E80"),sQuery(id+"F22.wireOp",EDGE,"E81"),sQuery(id+"F22.wireOp",EDGE,"E82"),sQuery(id+"F22.wireOp",EDGE,"E88")])],"isStart":false})});
            var sketch = newSketch(context, id + "F28", { "sketchPlane" : qUnion([Q0])});
            skLineSegment(sketch, "E91.0", {"start": v(212.76, -2.65) * mm, "end": v(207, -12.65) * mm});
            skLineSegment(sketch, "E91.1", {"start": v(191.74, -2.65) * mm, "end": v(212.76, -2.65) * mm});
            skLineSegment(sketch, "E91.2", {"start": v(197.5, -12.65) * mm, "end": v(191.74, -2.65) * mm});
            skLineSegment(sketch, "E92.0", {"start": v(49.56, -2.65) * mm, "end": v(43.8, -12.65) * mm});
            skLineSegment(sketch, "E92.1", {"start": v(49.56, -2.65) * mm, "end": v(28.54, -2.65) * mm});
            skLineSegment(sketch, "E92.2", {"start": v(28.54, -2.65) * mm, "end": v(34.3, -12.65) * mm});
            skLineSegment(sketch, "E93", {"start": v(34.3, -12.65) * mm, "end": v(43.8, -12.65) * mm});
            skLineSegment(sketch, "E94", {"start": v(207, -12.65) * mm, "end": v(197.5, -12.65) * mm});
            skSolve(sketch);
        }
        {
            var Q0;
            Q0 = qSketchRegion(id + "F28", true);
            var Q1;
            Q1=makeQuery(id+"F12.opExtrude","SWEPT_FACE",FACE,{"disambiguationData":[OSD([sQuery(id+"F10.wireOp",EDGE,"E41.0.1")])]});
            extrude(context, id + "F29", {"entities" : qUnion([Q0]), "endBound" : BoundingType.UP_TO_SURFACE, "endBoundEntityFace" : qUnion([Q1]), "depth" : 25 * mm});
        }
        {
            var Q0;
            Q0=makeQuery(id+"F29.opExtrude","SWEPT_FACE",FACE,{"disambiguationData":[OSD([sQuery(id+"F28.wireOp",EDGE,"E94")])]});
            var sketch = newSketch(context, id + "F30", { "sketchPlane" : qUnion([Q0])});
            skLineSegment(sketch, "E95.0.0", {"start": v(148.17, -43.8) * mm, "end": v(171.87, -43.8) * mm, "construction": true});
            skLineSegment(sketch, "E95.0.1", {"start": v(171.87, -43.8) * mm, "end": v(171.87, -34.3) * mm, "construction": true});
            skLineSegment(sketch, "E95.0.2", {"start": v(171.87, -34.3) * mm, "end": v(148.17, -34.3) * mm, "construction": true});
            skLineSegment(sketch, "E95.0.3", {"start": v(148.17, -34.3) * mm, "end": v(148.17, -43.8) * mm, "construction": true});
            skLineSegment(sketch, "E96.0.0", {"start": v(171.87, -207) * mm, "end": v(171.87, -197.5) * mm, "construction": true});
            skLineSegment(sketch, "E96.0.1", {"start": v(171.87, -197.5) * mm, "end": v(148.17, -197.5) * mm, "construction": true});
            skLineSegment(sketch, "E96.0.2", {"start": v(148.17, -197.5) * mm, "end": v(148.17, -207) * mm, "construction": true});
            skLineSegment(sketch, "E96.0.3", {"start": v(148.17, -207) * mm, "end": v(171.87, -207) * mm, "construction": true});
            skLineSegment(sketch, "E97.bottom", {"start": v(171.87, -207) * mm, "end": v(148.17, -207) * mm});
            skLineSegment(sketch, "E97.top", {"start": v(171.87, -34.3) * mm, "end": v(148.17, -34.3) * mm});
            skLineSegment(sketch, "E97.left", {"start": v(171.87, -207) * mm, "end": v(171.87, -34.3) * mm});
            skLineSegment(sketch, "E97.right", {"start": v(148.17, -207) * mm, "end": v(148.17, -34.3) * mm});
            skSolve(sketch);
        }
        {
            var Q0;
            Q0 = qSketchRegion(id + "F30", true);
            extrude(context, id + "F31", {"entities" : qUnion([Q0]), "operationType" : NewBodyOperationType.ADD, "depth" : 5 * mm});
        }
        {
            var Q0;
            Q0=makeQuery(id+"F31.opExtrude","CAP_FACE",FACE,{"disambiguationData":[OSD([sQuery(id+"F30.wireOp",EDGE,"E97.bottom"),sQuery(id+"F30.wireOp",EDGE,"E97.top"),sQuery(id+"F30.wireOp",EDGE,"E97.left"),sQuery(id+"F30.wireOp",EDGE,"E97.right")])],"isStart":false});
            var sketch = newSketch(context, id + "F32", { "sketchPlane" : qUnion([Q0])});
            skLineSegment(sketch, "E98", {"start": v(148.17, -34.3) * mm, "end": v(136.1, -34.3) * mm});
            skLineSegment(sketch, "E99", {"start": v(136.1, -34.3) * mm, "end": v(31.23, -115.13) * mm});
            skLineSegment(sketch, "E100", {"start": v(31.23, -115.13) * mm, "end": v(31.23, -126.17) * mm});
            skLineSegment(sketch, "E101", {"start": v(31.23, -126.17) * mm, "end": v(136.1, -207) * mm});
            skPoint(sketch, "E101.endSnap0", {"position": v(160.02, -207) * mm});
            skLineSegment(sketch, "E102", {"start": v(136.1, -207) * mm, "end": v(148.17, -207) * mm});
            skLineSegment(sketch, "E103.0", {"start": v(43.04, -118.65) * mm, "end": v(139.52, -44.3) * mm});
            skLineSegment(sketch, "E103.1", {"start": v(139.52, -197) * mm, "end": v(43.04, -122.65) * mm});
            skLineSegment(sketch, "E104", {"start": v(148.17, -197) * mm, "end": v(139.52, -197) * mm});
            skLineSegment(sketch, "E105", {"start": v(148.17, -207) * mm, "end": v(148.17, -197) * mm});
            skLineSegment(sketch, "E106", {"start": v(139.52, -44.3) * mm, "end": v(148.17, -44.3) * mm});
            skLineSegment(sketch, "E107", {"start": v(148.17, -44.3) * mm, "end": v(148.17, -34.3) * mm});
            skLineSegment(sketch, "E108", {"start": v(43.04, -118.65) * mm, "end": v(43.04, -122.65) * mm});
            skCircle(sketch, "E109.0", {"center": v(37.12, -120.65) * mm, "radius": 2.8 * mm, "construction": true});
            skSolve(sketch);
        }
        {
            var Q0;
            Q0 = qSketchRegion(id + "F32", true);
            var Q1;
            Q1=makeQuery(id+"F31.opExtrude","CAP_FACE",FACE,{"disambiguationData":[OSD([sQuery(id+"F30.wireOp",EDGE,"E97.bottom"),sQuery(id+"F30.wireOp",EDGE,"E97.top"),sQuery(id+"F30.wireOp",EDGE,"E97.left"),sQuery(id+"F30.wireOp",EDGE,"E97.right")])],"isStart":true});
            extrude(context, id + "F33", {"entities" : qUnion([Q0]), "operationType" : NewBodyOperationType.ADD, "endBound" : BoundingType.UP_TO_SURFACE, "oppositeDirection" : true, "endBoundEntityFace" : qUnion([Q1]), "depth" : 25 * mm});
        }
        {
            var Q0;
            Q0=makeQuery(id+"F33.opExtrude","SWEPT_EDGE",EDGE,{"disambiguationData":[OSD([sQuery(id+"F30.wireOp",EDGE,"E97.right"),sQuery(id+"F32.wireOp",EDGE,"E104"),sQuery(id+"F32.wireOp",EDGE,"E105")])]});
            var Q1;
            Q1=makeQuery(id+"F33.opExtrude","SWEPT_EDGE",EDGE,{"disambiguationData":[OSD([sQuery(id+"F30.wireOp",EDGE,"E97.right"),sQuery(id+"F32.wireOp",EDGE,"E106"),sQuery(id+"F32.wireOp",EDGE,"E107")])]});
            chamfer(context, id + "F34", {"entities" : qUnion([Q0, Q1]), "width" : 10 * mm, "tangentPropagation" : true});
        }
        {
            var Q0;
            Q0=makeQuery(id+"F34.opChamfer","BLEND_EDGE",EDGE,{"blendedFrom":[makeQuery(id+"F33.opExtrude","SWEPT_EDGE",EDGE,{"disambiguationData":[OSD([sQuery(id+"F30.wireOp",EDGE,"E97.right"),sQuery(id+"F32.wireOp",EDGE,"E106"),sQuery(id+"F32.wireOp",EDGE,"E107")])]}),makeQuery(id+"F33.opExtrude","SWEPT_FACE",FACE,{"disambiguationData":[OSD([sQuery(id+"F32.wireOp",EDGE,"E103.0")])]})],"blendedInto":[makeQuery(id+"F33.opExtrude","SWEPT_FACE",FACE,{"disambiguationData":[OSD([sQuery(id+"F32.wireOp",EDGE,"E103.0")])]})]});
            var Q1;
            {var subQ1=sQuery(id+"F32.wireOp",EDGE,"E107");var subQ2=sQuery(id+"F32.wireOp",EDGE,"E106");var subQ4=sQuery(id+"F32.wireOp",EDGE,"E104");var subQ12=sQuery(id+"F30.wireOp",EDGE,"E97.right");Q1=makeQuery(id+"F34.opChamfer","BLEND_EDGE",EDGE,{"blendedFrom":[makeQuery(id+"F33.opExtrude","SWEPT_EDGE",EDGE,{"disambiguationData":[OSD([subQ12,subQ2,subQ1])]}),makeQuery(id+"F33.boolean.opBoolean","SPLIT",FACE,{"disambiguationData":[TD([makeQuery(id+"F33.opExtrude","SWEPT_FACE",FACE,{"disambiguationData":[OSD([subQ4])]})])],"derivedFrom":makeQuery(id+"F31.boolean.opBoolean","MERGE",FACE,{"derivedFrom":[makeQuery(id+"F29.opExtrude","CAP_FACE",FACE,{"disambiguationData":[OSD([sQuery(id+"F28.wireOp",EDGE,"E91.0"),sQuery(id+"F28.wireOp",EDGE,"E91.1"),sQuery(id+"F28.wireOp",EDGE,"E91.2"),sQuery(id+"F28.wireOp",EDGE,"E94")])],"isStart":true}),makeQuery(id+"F29.opExtrude","CAP_FACE",FACE,{"disambiguationData":[OSD([sQuery(id+"F28.wireOp",EDGE,"E92.0"),sQuery(id+"F28.wireOp",EDGE,"E92.1"),sQuery(id+"F28.wireOp",EDGE,"E92.2"),sQuery(id+"F28.wireOp",EDGE,"E93")])],"isStart":true}),makeQuery(id+"F31.opExtrude","SWEPT_FACE",FACE,{"disambiguationData":[OSD([subQ12])]})]})})],"blendedInto":[makeQuery(id+"F33.boolean.opBoolean","SPLIT",FACE,{"disambiguationData":[TD([makeQuery(id+"F33.opExtrude","SWEPT_FACE",FACE,{"disambiguationData":[OSD([subQ4])]})])],"derivedFrom":makeQuery(id+"F31.boolean.opBoolean","MERGE",FACE,{"derivedFrom":[makeQuery(id+"F29.opExtrude","CAP_FACE",FACE,{"disambiguationData":[OSD([sQuery(id+"F28.wireOp",EDGE,"E91.0"),sQuery(id+"F28.wireOp",EDGE,"E91.1"),sQuery(id+"F28.wireOp",EDGE,"E91.2"),sQuery(id+"F28.wireOp",EDGE,"E94")])],"isStart":true}),makeQuery(id+"F29.opExtrude","CAP_FACE",FACE,{"disambiguationData":[OSD([sQuery(id+"F28.wireOp",EDGE,"E92.0"),sQuery(id+"F28.wireOp",EDGE,"E92.1"),sQuery(id+"F28.wireOp",EDGE,"E92.2"),sQuery(id+"F28.wireOp",EDGE,"E93")])],"isStart":true}),makeQuery(id+"F31.opExtrude","SWEPT_FACE",FACE,{"disambiguationData":[OSD([subQ12])]})]})})]});}
            var Q2;
            Q2=makeQuery(id+"F34.opChamfer","BLEND_EDGE",EDGE,{"blendedFrom":[makeQuery(id+"F33.opExtrude","SWEPT_EDGE",EDGE,{"disambiguationData":[OSD([sQuery(id+"F30.wireOp",EDGE,"E97.right"),sQuery(id+"F32.wireOp",EDGE,"E104"),sQuery(id+"F32.wireOp",EDGE,"E105")])]}),makeQuery(id+"F33.opExtrude","SWEPT_FACE",FACE,{"disambiguationData":[OSD([sQuery(id+"F32.wireOp",EDGE,"E103.1")])]})],"blendedInto":[makeQuery(id+"F33.opExtrude","SWEPT_FACE",FACE,{"disambiguationData":[OSD([sQuery(id+"F32.wireOp",EDGE,"E103.1")])]})]});
            var Q3;
            {var subQ3=sQuery(id+"F32.wireOp",EDGE,"E105");var subQ4=sQuery(id+"F32.wireOp",EDGE,"E104");var subQ12=sQuery(id+"F30.wireOp",EDGE,"E97.right");Q3=makeQuery(id+"F34.opChamfer","BLEND_EDGE",EDGE,{"blendedFrom":[makeQuery(id+"F33.opExtrude","SWEPT_EDGE",EDGE,{"disambiguationData":[OSD([subQ12,subQ4,subQ3])]}),makeQuery(id+"F33.boolean.opBoolean","SPLIT",FACE,{"disambiguationData":[TD([makeQuery(id+"F33.opExtrude","SWEPT_FACE",FACE,{"disambiguationData":[OSD([subQ4])]})])],"derivedFrom":makeQuery(id+"F31.boolean.opBoolean","MERGE",FACE,{"derivedFrom":[makeQuery(id+"F29.opExtrude","CAP_FACE",FACE,{"disambiguationData":[OSD([sQuery(id+"F28.wireOp",EDGE,"E91.0"),sQuery(id+"F28.wireOp",EDGE,"E91.1"),sQuery(id+"F28.wireOp",EDGE,"E91.2"),sQuery(id+"F28.wireOp",EDGE,"E94")])],"isStart":true}),makeQuery(id+"F29.opExtrude","CAP_FACE",FACE,{"disambiguationData":[OSD([sQuery(id+"F28.wireOp",EDGE,"E92.0"),sQuery(id+"F28.wireOp",EDGE,"E92.1"),sQuery(id+"F28.wireOp",EDGE,"E92.2"),sQuery(id+"F28.wireOp",EDGE,"E93")])],"isStart":true}),makeQuery(id+"F31.opExtrude","SWEPT_FACE",FACE,{"disambiguationData":[OSD([subQ12])]})]})})],"blendedInto":[makeQuery(id+"F33.boolean.opBoolean","SPLIT",FACE,{"disambiguationData":[TD([makeQuery(id+"F33.opExtrude","SWEPT_FACE",FACE,{"disambiguationData":[OSD([subQ4])]})])],"derivedFrom":makeQuery(id+"F31.boolean.opBoolean","MERGE",FACE,{"derivedFrom":[makeQuery(id+"F29.opExtrude","CAP_FACE",FACE,{"disambiguationData":[OSD([sQuery(id+"F28.wireOp",EDGE,"E91.0"),sQuery(id+"F28.wireOp",EDGE,"E91.1"),sQuery(id+"F28.wireOp",EDGE,"E91.2"),sQuery(id+"F28.wireOp",EDGE,"E94")])],"isStart":true}),makeQuery(id+"F29.opExtrude","CAP_FACE",FACE,{"disambiguationData":[OSD([sQuery(id+"F28.wireOp",EDGE,"E92.0"),sQuery(id+"F28.wireOp",EDGE,"E92.1"),sQuery(id+"F28.wireOp",EDGE,"E92.2"),sQuery(id+"F28.wireOp",EDGE,"E93")])],"isStart":true}),makeQuery(id+"F31.opExtrude","SWEPT_FACE",FACE,{"disambiguationData":[OSD([subQ12])]})]})})]});}
            var Q4;
            Q4=makeQuery(id+"F33.opExtrude","SWEPT_EDGE",EDGE,{"disambiguationData":[OSD([sQuery(id+"F32.wireOp",EDGE,"E100"),sQuery(id+"F32.wireOp",EDGE,"E101")])]});
            var Q5;
            Q5=makeQuery(id+"F33.opExtrude","SWEPT_EDGE",EDGE,{"disambiguationData":[OSD([sQuery(id+"F32.wireOp",EDGE,"E99"),sQuery(id+"F32.wireOp",EDGE,"E100")])]});
            fillet(context, id + "F35", {"entities" : qUnion([Q0, Q1, Q2, Q3, Q4, Q5]), "radius" : 10 * mm, "tangentPropagation" : true, "allowEdgeOverflow" : false});
        }
        {
            var Q0;
            Q0=makeQuery(id+"F33.opExtrude","SWEPT_EDGE",EDGE,{"disambiguationData":[OSD([sQuery(id+"F32.wireOp",EDGE,"E103.1"),sQuery(id+"F32.wireOp",EDGE,"E108")])]});
            var Q1;
            Q1=makeQuery(id+"F33.opExtrude","SWEPT_EDGE",EDGE,{"disambiguationData":[OSD([sQuery(id+"F32.wireOp",EDGE,"E103.0"),sQuery(id+"F32.wireOp",EDGE,"E108")])]});
            fillet(context, id + "F36", {"entities" : qUnion([Q0, Q1]), "radius" : 5 * mm, "tangentPropagation" : true, "allowEdgeOverflow" : false});
        }
        {
            var Q0;
            Q0=makeQuery(id+"F33.boolean.opBoolean","MERGE",FACE,{"derivedFrom":[makeQuery(id+"F31.opExtrude","SWEPT_FACE",FACE,{"disambiguationData":[OSD([sQuery(id+"F30.wireOp",EDGE,"E97.top")])]}),makeQuery(id+"F33.opExtrude","SWEPT_FACE",FACE,{"disambiguationData":[OSD([sQuery(id+"F32.wireOp",EDGE,"E98")])]})]});
            var sketch = newSketch(context, id + "F37", { "sketchPlane" : qUnion([Q0])});
            skLineSegment(sketch, "E110", {"start": v(171.87, -12.65) * mm, "end": v(166.87, -17.65) * mm});
            skLineSegment(sketch, "E111", {"start": v(166.87, -17.65) * mm, "end": v(171.87, -17.65) * mm});
            skLineSegment(sketch, "E112", {"start": v(171.87, -12.65) * mm, "end": v(171.87, -17.65) * mm});
            skLineSegment(sketch, "E113.0.1", {"start": v(171.87, -12.65) * mm, "end": v(181.87, -2.65) * mm});
            skLineSegment(sketch, "E113.0.3", {"start": v(181.87, -2.65) * mm, "end": v(171.87, -12.65) * mm});
            skSolve(sketch);
        }
        {
            var Q0;
            Q0=makeQuery(id+"F37.imprint","IMPRINT",FACE,{"disambiguationData":[TD([[makeQuery(id+"F37.imprint","IMPRINT",EDGE,{"derivedFrom":sQuery(id+"F37.wireOp",EDGE,"E110")}),1.0]])]});
            extrude(context, id + "F38", {"entities" : qUnion([Q0]), "operationType" : NewBodyOperationType.REMOVE, "endBound" : BoundingType.THROUGH_ALL, "oppositeDirection" : true, "depth" : 25 * mm});
        }
        {
            var Q0;
            Q0=makeQuery(id+"F31.opExtrude","CAP_EDGE",EDGE,{"disambiguationData":[OSD([sQuery(id+"F30.wireOp",EDGE,"E97.bottom")])],"isStart":false});
            var Q1;
            Q1=makeQuery(id+"F31.opExtrude","CAP_EDGE",EDGE,{"disambiguationData":[OSD([sQuery(id+"F30.wireOp",EDGE,"E97.top")])],"isStart":false});
            chamfer(context, id + "F39", {"entities" : qUnion([Q0, Q1]), "width" : 5 * mm, "tangentPropagation" : true});
        }
        {
            var Q0;
            {var subQ0=sQuery(id+"F32.wireOp",EDGE,"E100");var subQ1=sQuery(id+"F32.wireOp",EDGE,"E99");Q0=makeQuery(id+"F35.opFillet","BLEND_EDGE",EDGE,{"blendedFrom":[makeQuery(id+"F33.opExtrude","SWEPT_EDGE",EDGE,{"disambiguationData":[OSD([subQ1,subQ0])]}),makeQuery(id+"F33.boolean.opBoolean","MERGE",FACE,{"derivedFrom":[makeQuery(id+"F31.opExtrude","CAP_FACE",FACE,{"disambiguationData":[OSD([sQuery(id+"F30.wireOp",EDGE,"E97.bottom"),sQuery(id+"F30.wireOp",EDGE,"E97.top"),sQuery(id+"F30.wireOp",EDGE,"E97.left"),sQuery(id+"F30.wireOp",EDGE,"E97.right")])],"isStart":false}),makeQuery(id+"F33.opExtrude","CAP_FACE",FACE,{"disambiguationData":[OSD([sQuery(id+"F32.wireOp",EDGE,"E98"),subQ1,subQ0,sQuery(id+"F32.wireOp",EDGE,"E101"),sQuery(id+"F32.wireOp",EDGE,"E102"),sQuery(id+"F32.wireOp",EDGE,"E103.0"),sQuery(id+"F32.wireOp",EDGE,"E103.1"),sQuery(id+"F32.wireOp",EDGE,"E104"),sQuery(id+"F32.wireOp",EDGE,"E105"),sQuery(id+"F32.wireOp",EDGE,"E106"),sQuery(id+"F32.wireOp",EDGE,"E107"),sQuery(id+"F32.wireOp",EDGE,"E108")])],"isStart":true})]})],"blendedInto":[makeQuery(id+"F33.boolean.opBoolean","MERGE",FACE,{"derivedFrom":[makeQuery(id+"F31.opExtrude","CAP_FACE",FACE,{"disambiguationData":[OSD([sQuery(id+"F30.wireOp",EDGE,"E97.bottom"),sQuery(id+"F30.wireOp",EDGE,"E97.top"),sQuery(id+"F30.wireOp",EDGE,"E97.left"),sQuery(id+"F30.wireOp",EDGE,"E97.right")])],"isStart":false}),makeQuery(id+"F33.opExtrude","CAP_FACE",FACE,{"disambiguationData":[OSD([sQuery(id+"F32.wireOp",EDGE,"E98"),subQ1,subQ0,sQuery(id+"F32.wireOp",EDGE,"E101"),sQuery(id+"F32.wireOp",EDGE,"E102"),sQuery(id+"F32.wireOp",EDGE,"E103.0"),sQuery(id+"F32.wireOp",EDGE,"E103.1"),sQuery(id+"F32.wireOp",EDGE,"E104"),sQuery(id+"F32.wireOp",EDGE,"E105"),sQuery(id+"F32.wireOp",EDGE,"E106"),sQuery(id+"F32.wireOp",EDGE,"E107"),sQuery(id+"F32.wireOp",EDGE,"E108")])],"isStart":true})]})]});}
            var Q1;
            {var subQ0=sQuery(id+"F32.wireOp",EDGE,"E107");var subQ1=sQuery(id+"F32.wireOp",EDGE,"E106");var subQ2=sQuery(id+"F32.wireOp",EDGE,"E103.0");var subQ3=sQuery(id+"F30.wireOp",EDGE,"E97.right");Q1=makeQuery(id+"F35.opFillet","BLEND_EDGE",EDGE,{"blendedFrom":[makeQuery(id+"F34.opChamfer","BLEND_EDGE",EDGE,{"blendedFrom":[makeQuery(id+"F33.opExtrude","SWEPT_EDGE",EDGE,{"disambiguationData":[OSD([subQ3,subQ1,subQ0])]}),makeQuery(id+"F33.opExtrude","SWEPT_FACE",FACE,{"disambiguationData":[OSD([subQ2])]})],"blendedInto":[makeQuery(id+"F33.opExtrude","SWEPT_FACE",FACE,{"disambiguationData":[OSD([subQ2])]})]}),makeQuery(id+"F33.boolean.opBoolean","MERGE",FACE,{"derivedFrom":[makeQuery(id+"F31.opExtrude","CAP_FACE",FACE,{"disambiguationData":[OSD([sQuery(id+"F30.wireOp",EDGE,"E97.bottom"),sQuery(id+"F30.wireOp",EDGE,"E97.top"),sQuery(id+"F30.wireOp",EDGE,"E97.left"),subQ3])],"isStart":false}),makeQuery(id+"F33.opExtrude","CAP_FACE",FACE,{"disambiguationData":[OSD([sQuery(id+"F32.wireOp",EDGE,"E98"),sQuery(id+"F32.wireOp",EDGE,"E99"),sQuery(id+"F32.wireOp",EDGE,"E100"),sQuery(id+"F32.wireOp",EDGE,"E101"),sQuery(id+"F32.wireOp",EDGE,"E102"),subQ2,sQuery(id+"F32.wireOp",EDGE,"E103.1"),sQuery(id+"F32.wireOp",EDGE,"E104"),sQuery(id+"F32.wireOp",EDGE,"E105"),subQ1,subQ0,sQuery(id+"F32.wireOp",EDGE,"E108")])],"isStart":true})]})],"blendedInto":[makeQuery(id+"F33.boolean.opBoolean","MERGE",FACE,{"derivedFrom":[makeQuery(id+"F31.opExtrude","CAP_FACE",FACE,{"disambiguationData":[OSD([sQuery(id+"F30.wireOp",EDGE,"E97.bottom"),sQuery(id+"F30.wireOp",EDGE,"E97.top"),sQuery(id+"F30.wireOp",EDGE,"E97.left"),subQ3])],"isStart":false}),makeQuery(id+"F33.opExtrude","CAP_FACE",FACE,{"disambiguationData":[OSD([sQuery(id+"F32.wireOp",EDGE,"E98"),sQuery(id+"F32.wireOp",EDGE,"E99"),sQuery(id+"F32.wireOp",EDGE,"E100"),sQuery(id+"F32.wireOp",EDGE,"E101"),sQuery(id+"F32.wireOp",EDGE,"E102"),subQ2,sQuery(id+"F32.wireOp",EDGE,"E103.1"),sQuery(id+"F32.wireOp",EDGE,"E104"),sQuery(id+"F32.wireOp",EDGE,"E105"),subQ1,subQ0,sQuery(id+"F32.wireOp",EDGE,"E108")])],"isStart":true})]})]});}
            chamfer(context, id + "F40", {"entities" : qUnion([Q0, Q1]), "width" : 2.5 * mm, "tangentPropagation" : true});
        }
        {
            var Q0;
            Q0=makeQuery(id+"F33.boolean.opBoolean","MERGE",FACE,{"derivedFrom":[makeQuery(id+"F31.opExtrude","CAP_FACE",FACE,{"disambiguationData":[OSD([sQuery(id+"F30.wireOp",EDGE,"E97.bottom"),sQuery(id+"F30.wireOp",EDGE,"E97.top"),sQuery(id+"F30.wireOp",EDGE,"E97.left"),sQuery(id+"F30.wireOp",EDGE,"E97.right")])],"isStart":false}),makeQuery(id+"F33.opExtrude","CAP_FACE",FACE,{"disambiguationData":[OSD([sQuery(id+"F32.wireOp",EDGE,"E98"),sQuery(id+"F32.wireOp",EDGE,"E99"),sQuery(id+"F32.wireOp",EDGE,"E100"),sQuery(id+"F32.wireOp",EDGE,"E101"),sQuery(id+"F32.wireOp",EDGE,"E102"),sQuery(id+"F32.wireOp",EDGE,"E103.0"),sQuery(id+"F32.wireOp",EDGE,"E103.1"),sQuery(id+"F32.wireOp",EDGE,"E104"),sQuery(id+"F32.wireOp",EDGE,"E105"),sQuery(id+"F32.wireOp",EDGE,"E106"),sQuery(id+"F32.wireOp",EDGE,"E107"),sQuery(id+"F32.wireOp",EDGE,"E108")])],"isStart":true})]});
            var sketch = newSketch(context, id + "F41", { "sketchPlane" : qUnion([Q0])});
            skCircle(sketch, "E114.0", {"center": v(37.12, -120.65) * mm, "radius": 2.8 * mm, "construction": true});
            skCircle(sketch, "E115.cCircle", {"center": v(37.12, -120.65) * mm, "radius": 3.95 * mm, "construction": true});
            skLineSegment(sketch, "E115.0", {"start": v(41.07, -118.37) * mm, "end": v(41.07, -122.93) * mm});
            skLineSegment(sketch, "E115.1", {"start": v(41.07, -122.93) * mm, "end": v(37.12, -125.21) * mm});
            skLineSegment(sketch, "E115.2", {"start": v(37.12, -125.21) * mm, "end": v(33.17, -122.93) * mm});
            skLineSegment(sketch, "E115.3", {"start": v(33.17, -122.93) * mm, "end": v(33.17, -118.37) * mm});
            skLineSegment(sketch, "E115.4", {"start": v(33.17, -118.37) * mm, "end": v(37.12, -116.09) * mm});
            skLineSegment(sketch, "E115.5", {"start": v(37.12, -116.09) * mm, "end": v(41.07, -118.37) * mm});
            skPoint(sketch, "E115.0.midPoint", {"position": v(41.07, -120.65) * mm});
            skSolve(sketch);
        }
        {
            var Q0;
            Q0 = qSketchRegion(id + "F41", true);
            extrude(context, id + "F42", {"entities" : qUnion([Q0]), "operationType" : NewBodyOperationType.REMOVE, "oppositeDirection" : true, "depth" : 2 * mm});
        }
        {
            var Q0;
            Q0=makeQuery(id+"F42.boolean.opBoolean","COPY",FACE,{"derivedFrom":makeQuery(id+"F42.opExtrude","CAP_FACE",FACE,{"disambiguationData":[OSD([sQuery(id+"F41.wireOp",EDGE,"E115.0"),sQuery(id+"F41.wireOp",EDGE,"E115.1"),sQuery(id+"F41.wireOp",EDGE,"E115.2"),sQuery(id+"F41.wireOp",EDGE,"E115.3"),sQuery(id+"F41.wireOp",EDGE,"E115.4"),sQuery(id+"F41.wireOp",EDGE,"E115.5")])],"isStart":false})});
            var sketch = newSketch(context, id + "F43", { "sketchPlane" : qUnion([Q0])});
            skCircle(sketch, "E116.0", {"center": v(37.12, -120.65) * mm, "radius": 2.8 * mm});
            skSolve(sketch);
        }
        {
            var Q0;
            Q0=makeQuery(id+"F43.imprint","IMPRINT",FACE,{"disambiguationData":[TD([[makeQuery(id+"F43.imprint","IMPRINT",EDGE,{"derivedFrom":sQuery(id+"F43.wireOp",EDGE,"E116.0")}),1.0]])]});
            extrude(context, id + "F44", {"entities" : qUnion([Q0]), "operationType" : NewBodyOperationType.REMOVE, "endBound" : BoundingType.THROUGH_ALL, "oppositeDirection" : true, "depth" : 25 * mm});
        }
        {
            var Q0;
            Q0=makeQuery(id+"F12.opExtrude","SWEPT_FACE",FACE,{"disambiguationData":[OSD([sQuery(id+"F10.wireOp",EDGE,"E41.0.5")])]});
            var Q1;
            Q1=makeQuery(id+"F11.opExtrude","SWEPT_FACE",FACE,{"disambiguationData":[OSD([sQuery(id+"F9.wireOp",EDGE,"E36")])]});
            extrude(context, id + "F45", {"entities" : qUnion([Q0, Q1]), "operationType" : NewBodyOperationType.ADD, "depth" : 2.5 * mm});
        }
    });
